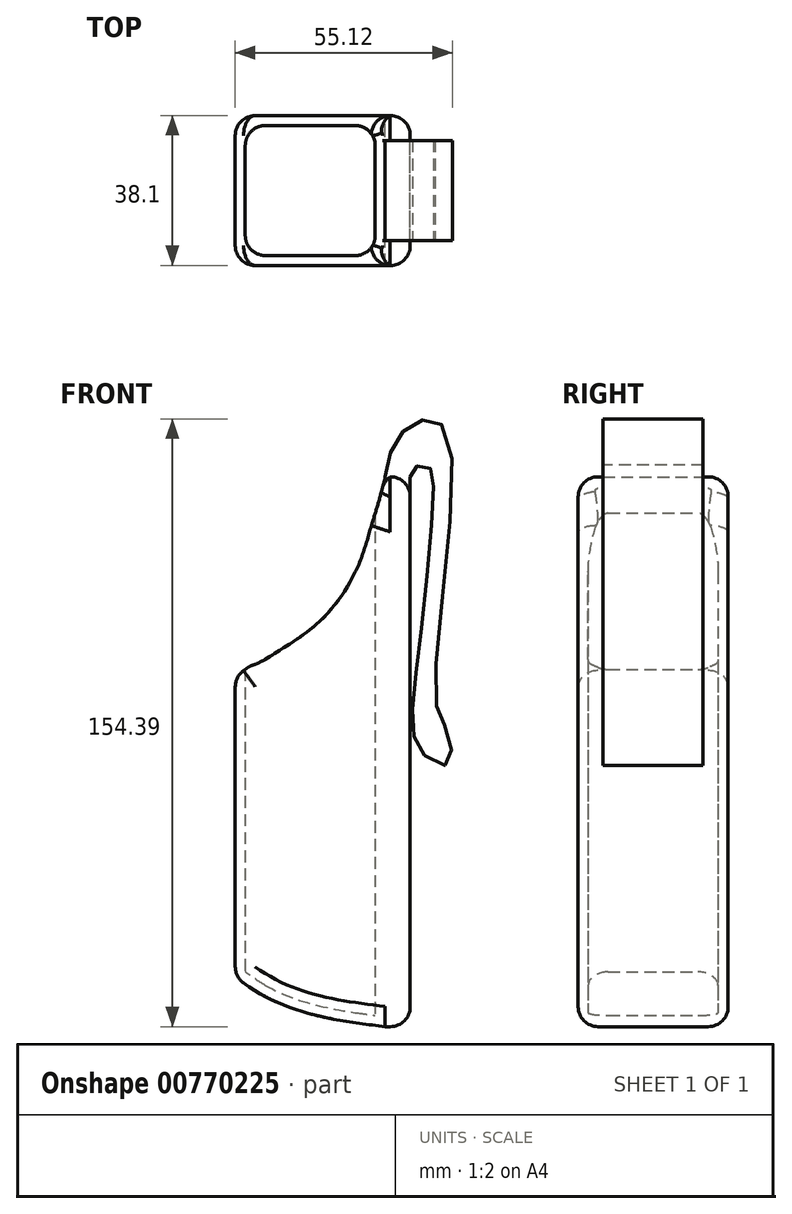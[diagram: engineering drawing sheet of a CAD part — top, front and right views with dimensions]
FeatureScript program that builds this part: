
annotation { "Feature Type Name" : "Feature", "Feature Type Description" : "" }
export const myFeature = defineFeature(function(context is Context, id is Id, definition is map)
    precondition{}
    {
        {
            var Q0;
            Q0=qCreatedBy(makeId("Front.planeOp"),FACE);
            var sketch = newSketch(context, id + "F0", { "sketchPlane" : qUnion([Q0])});
            skPoint(sketch, "E0.middle", {"position": v(0, 0) * mm});
            skLineSegment(sketch, "E1.top", {"start": v(0, 88.9) * mm, "end": v(-38.1, 88.9) * mm});
            skLineSegment(sketch, "E1.left", {"start": v(0, 0) * mm, "end": v(0, 88.9) * mm});
            skLineSegment(sketch, "E2.bottom", {"start": v(-38.1, 88.9) * mm, "end": v(0, 88.9) * mm});
            skLineSegment(sketch, "E2.top", {"start": v(-38.1, 12.7) * mm, "end": v(0, 12.7) * mm});
            skLineSegment(sketch, "E2.left", {"start": v(-38.1, 88.9) * mm, "end": v(-38.1, 12.7) * mm});
            skLineSegment(sketch, "E2.right", {"start": v(0, 88.9) * mm, "end": v(0, 12.7) * mm});
            skFitSpline(sketch, "E3", {"points": [v(-38.1, 12.7) * mm, v(0, 0) * mm], "startDerivative": vector(33.56, -27.29) * mm, "endDerivative": vector(44.12, -5.36) * mm});
            skFitSpline(sketch, "E4", {"points": [v(0, 139.7) * mm, v(-38.1, 88.9) * mm], "startDerivative": vector(-29.94, -120.33) * mm, "endDerivative": vector(-50.86, -39.17) * mm});
            skLineSegment(sketch, "E5", {"start": v(0, 139.7) * mm, "end": v(0, 88.9) * mm});
            skSolve(sketch);
        }
        {
            var Q0;
            Q0=qCreatedBy(makeId("Front.planeOp"),FACE);
            var sketch = newSketch(context, id + "F1", { "sketchPlane" : qUnion([Q0])});
            skLineSegment(sketch, "E6.bottom", {"start": v(0, 0) * mm, "end": v(6.35, 0) * mm});
            skLineSegment(sketch, "E6.top", {"start": v(0, 139.7) * mm, "end": v(6.35, 139.7) * mm});
            skLineSegment(sketch, "E6.left", {"start": v(0, 0) * mm, "end": v(0, 139.7) * mm});
            skLineSegment(sketch, "E6.right", {"start": v(6.35, 0) * mm, "end": v(6.35, 139.7) * mm});
            skFitSpline(sketch, "E7", {"points": [v(0, 139.7) * mm, v(3, 149.37) * mm, v(10.06, 154.31) * mm, v(16.18, 149.37) * mm, v(12.65, 83.9) * mm, v(15.48, 75.66) * mm, v(16.18, 66.71) * mm, v(9.83, 69.07) * mm, v(6.89, 77.28) * mm, v(9.41, 103.27) * mm, v(12.3, 138.54) * mm, v(11.08, 142.16) * mm, v(7.74, 142.31) * mm, v(6.35, 139.7) * mm], "startDerivative": vector(24.86, 146.16) * mm, "endDerivative": vector(-21.88, -73.83) * mm});
            skSolve(sketch);
        }
        {
            var Q0;
            Q0 = qSketchRegion(id + "F0", true);
            extrude(context, id + "F2", {"entities" : qUnion([Q0]), "endBound" : BoundingType.SYMMETRIC, "depth" : 38.1 * mm, "offsetDistance" : 25.4 * mm});
        }
        {
            var Q0;
            Q0=makeQuery(id+"F2.opExtrude","SWEPT_FACE",FACE,{"disambiguationData":[OSD([sQuery(id+"F0.wireOp",EDGE,"E4")])]});
            shell(context, id + "F3", {"entities" : qUnion([Q0]), "thickness" : 2.54 * mm});
        }
        {
            var Q0;
            Q0=makeQuery(id+"F2.opExtrude","CAP_EDGE",EDGE,{"disambiguationData":[OSD([sQuery(id+"F0.wireOp",EDGE,"E2.left")])],"isStart":true});
            var Q1;
            Q1=makeQuery(id+"F2.opExtrude","CAP_EDGE",EDGE,{"disambiguationData":[OSD([sQuery(id+"F0.wireOp",EDGE,"E2.left")])],"isStart":false});
            var Q2;
            Q2=makeQuery(id+"F2.opExtrude","SWEPT_EDGE",EDGE,{"disambiguationData":[OSD([sQuery(id+"F0.wireOp",EDGE,"E2.bottom"),sQuery(id+"F0.wireOp",EDGE,"E2.left"),sQuery(id+"F0.wireOp",EDGE,"E4")])]});
            var Q3;
            Q3=makeQuery(id+"F2.opExtrude","CAP_EDGE",EDGE,{"disambiguationData":[OSD([sQuery(id+"F0.wireOp",EDGE,"E3")])],"isStart":true});
            var Q4;
            Q4=makeQuery(id+"F2.opExtrude","CAP_EDGE",EDGE,{"disambiguationData":[OSD([sQuery(id+"F0.wireOp",EDGE,"E3")])],"isStart":false});
            var Q5;
            Q5=makeQuery(id+"F2.opExtrude","SWEPT_EDGE",EDGE,{"disambiguationData":[OSD([sQuery(id+"F0.wireOp",EDGE,"E2.top"),sQuery(id+"F0.wireOp",EDGE,"E2.left"),sQuery(id+"F0.wireOp",EDGE,"E3")])]});
            var Q6;
            {var subQ0=sQuery(id+"F0.wireOp",EDGE,"E5");var subQ1=sQuery(id+"F0.wireOp",EDGE,"E2.right");var subQ2=sQuery(id+"F0.wireOp",EDGE,"E1.left");Q6=makeQuery(id+"F3.opShell","OFFSET_EDGE",EDGE,{"disambiguationData":[OSD([subQ2,subQ1,subQ0]),TDD([makeQuery(id+"F2.opExtrude","CAP_EDGE",EDGE,{"disambiguationData":[OSD([subQ2,subQ1,subQ0])],"isStart":true})])]});}
            var Q7;
            {var subQ0=sQuery(id+"F0.wireOp",EDGE,"E5");var subQ1=sQuery(id+"F0.wireOp",EDGE,"E2.right");var subQ2=sQuery(id+"F0.wireOp",EDGE,"E1.left");Q7=makeQuery(id+"F3.opShell","OFFSET_EDGE",EDGE,{"disambiguationData":[OSD([subQ2,subQ1,subQ0]),TDD([makeQuery(id+"F2.opExtrude","CAP_EDGE",EDGE,{"disambiguationData":[OSD([subQ2,subQ1,subQ0])],"isStart":false})])]});}
            var Q8;
            {var subQ0=sQuery(id+"F0.wireOp",EDGE,"E2.left");Q8=makeQuery(id+"F3.opShell","OFFSET_EDGE",EDGE,{"disambiguationData":[OSD([subQ0]),TDD([makeQuery(id+"F2.opExtrude","CAP_EDGE",EDGE,{"disambiguationData":[OSD([subQ0])],"isStart":false})])]});}
            var Q9;
            {var subQ0=sQuery(id+"F0.wireOp",EDGE,"E2.left");Q9=makeQuery(id+"F3.opShell","OFFSET_EDGE",EDGE,{"disambiguationData":[OSD([subQ0]),TDD([makeQuery(id+"F2.opExtrude","CAP_EDGE",EDGE,{"disambiguationData":[OSD([subQ0])],"isStart":true})])]});}
            fillet(context, id + "F4", {"entities" : qUnion([Q0, Q1, Q2, Q3, Q4, Q5, Q6, Q7, Q8, Q9]), "radius" : 5.08 * mm, "tangentPropagation" : true, "allowEdgeOverflow" : false});
        }
        {
            var Q0;
            Q0=makeQuery(id+"F1.imprint","IMPRINT",FACE,{"disambiguationData":[TD([[makeQuery(id+"F1.imprint","IMPRINT",EDGE,{"derivedFrom":sQuery(id+"F1.wireOp",EDGE,"E6.bottom")}),1.0]])]});
            extrude(context, id + "F5", {"entities" : qUnion([Q0]), "operationType" : NewBodyOperationType.ADD, "endBound" : BoundingType.SYMMETRIC, "depth" : 38.1 * mm, "offsetDistance" : 25.4 * mm});
        }
        {
            var Q0;
            Q0=makeQuery(id+"F5.opExtrude","CAP_EDGE",EDGE,{"disambiguationData":[OSD([sQuery(id+"F1.wireOp",EDGE,"E6.bottom")])],"isStart":false});
            var Q1;
            Q1=makeQuery(id+"F5.opExtrude","CAP_EDGE",EDGE,{"disambiguationData":[OSD([sQuery(id+"F1.wireOp",EDGE,"E6.bottom")])],"isStart":true});
            var Q2;
            Q2=makeQuery(id+"F5.opExtrude","CAP_EDGE",EDGE,{"disambiguationData":[OSD([sQuery(id+"F1.wireOp",EDGE,"E6.right")])],"isStart":false});
            var Q3;
            Q3=makeQuery(id+"F5.opExtrude","CAP_EDGE",EDGE,{"disambiguationData":[OSD([sQuery(id+"F1.wireOp",EDGE,"E6.right")])],"isStart":true});
            var Q4;
            Q4=makeQuery(id+"F5.opExtrude","SWEPT_EDGE",EDGE,{"disambiguationData":[OSD([sQuery(id+"F1.wireOp",EDGE,"E6.bottom"),sQuery(id+"F1.wireOp",EDGE,"E6.right")])]});
            fillet(context, id + "F6", {"entities" : qUnion([Q0, Q1, Q2, Q3, Q4]), "radius" : 5.08 * mm, "tangentPropagation" : true, "allowEdgeOverflow" : false});
        }
        {
            var Q0;
            Q0=makeQuery(id+"F1.imprint","IMPRINT",FACE,{"disambiguationData":[TD([[makeQuery(id+"F1.imprint","IMPRINT",EDGE,{"derivedFrom":sQuery(id+"F1.wireOp",EDGE,"E6.top")}),1.0]])]});
            extrude(context, id + "F7", {"entities" : qUnion([Q0]), "operationType" : NewBodyOperationType.ADD, "endBound" : BoundingType.SYMMETRIC, "depth" : 25.4 * mm, "offsetDistance" : 25.4 * mm});
        }
        {
            var Q0;
            Q0=makeQuery(id+"F6.opFillet","BLEND_EDGE",EDGE,{"blendedFrom":[makeQuery(id+"F5.opExtrude","CAP_EDGE",EDGE,{"disambiguationData":[OSD([sQuery(id+"F1.wireOp",EDGE,"E6.right")])],"isStart":false}),makeQuery(id+"F5.opExtrude","SWEPT_FACE",FACE,{"disambiguationData":[OSD([sQuery(id+"F1.wireOp",EDGE,"E6.top")])]})],"blendedInto":[makeQuery(id+"F5.opExtrude","SWEPT_FACE",FACE,{"disambiguationData":[OSD([sQuery(id+"F1.wireOp",EDGE,"E6.top")])]})]});
            var Q1;
            Q1=makeQuery(id+"F6.opFillet","BLEND_EDGE",EDGE,{"blendedFrom":[makeQuery(id+"F5.opExtrude","CAP_EDGE",EDGE,{"disambiguationData":[OSD([sQuery(id+"F1.wireOp",EDGE,"E6.right")])],"isStart":true}),makeQuery(id+"F5.opExtrude","SWEPT_FACE",FACE,{"disambiguationData":[OSD([sQuery(id+"F1.wireOp",EDGE,"E6.top")])]})],"blendedInto":[makeQuery(id+"F5.opExtrude","SWEPT_FACE",FACE,{"disambiguationData":[OSD([sQuery(id+"F1.wireOp",EDGE,"E6.top")])]})]});
            fillet(context, id + "F8", {"entities" : qUnion([Q0, Q1]), "radius" : 5.08 * mm, "tangentPropagation" : true, "allowEdgeOverflow" : false});
        }
        {
            var Q0;
            Q0=makeQuery(id+"F2.opExtrude","CAP_EDGE",EDGE,{"disambiguationData":[OSD([sQuery(id+"F0.wireOp",EDGE,"E4")])],"isStart":true});
            var Q1;
            Q1=makeQuery(id+"F2.opExtrude","CAP_EDGE",EDGE,{"disambiguationData":[OSD([sQuery(id+"F0.wireOp",EDGE,"E4")])],"isStart":false});
            fillet(context, id + "F9", {"entities" : qUnion([Q0, Q1]), "radius" : 5.08 * mm, "tangentPropagation" : true, "allowEdgeOverflow" : false});
        }
    });
